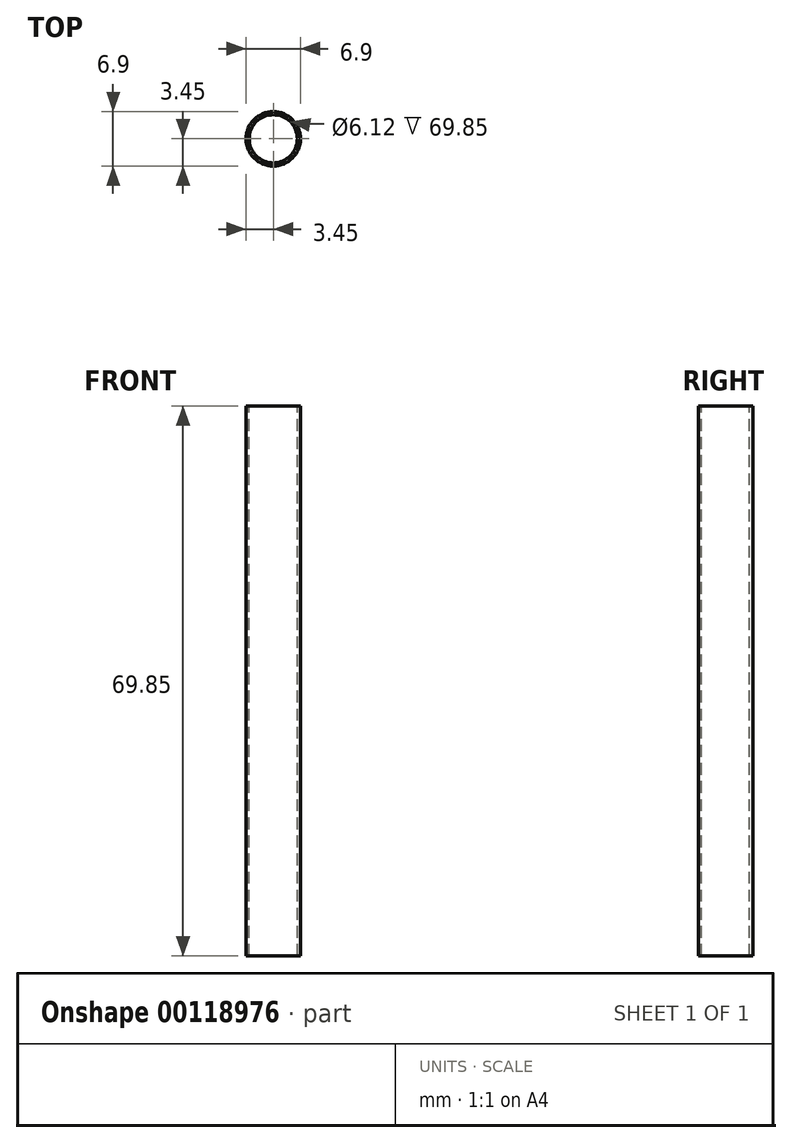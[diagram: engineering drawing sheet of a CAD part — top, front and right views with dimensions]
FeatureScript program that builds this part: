
annotation { "Feature Type Name" : "Feature", "Feature Type Description" : "" }
export const myFeature = defineFeature(function(context is Context, id is Id, definition is map)
    precondition{}
    {
        {
            var Q0;
            Q0=qCreatedBy(makeId("Top.planeOp"),FACE);
            var sketch = newSketch(context, id + "F0", { "sketchPlane" : qUnion([Q0])});
            skCircle(sketch, "E0", {"center": v(0, 0) * mm, "radius": 3.45 * mm});
            skSolve(sketch);
        }
        {
            var Q0;
            Q0=makeQuery(id+"F0.imprint","IMPRINT",FACE,{"disambiguationData":[TD([[makeQuery(id+"F0.imprint","IMPRINT",EDGE,{"derivedFrom":sQuery(id+"F0.wireOp",EDGE,"E0")}),1.0]])]});
            var Q1;
            Q1=sQuery(id+"F0.wireOp",EDGE,"E0");
            extrude(context, id + "F1", {"entities" : qUnion([Q0]), "surfaceEntities" : qUnion([Q1]), "depth" : 69.85 * mm});
        }
        {
            var Q0;
            Q0=makeQuery(id+"F1.opExtrude","CAP_FACE",FACE,{"disambiguationData":[OSD([sQuery(id+"F0.wireOp",EDGE,"E0")])],"isStart":false});
            var sketch = newSketch(context, id + "F2", { "sketchPlane" : qUnion([Q0])});
            skCircle(sketch, "E1", {"center": v(0, 0) * mm, "radius": 3.06 * mm});
            skSolve(sketch);
        }
        {
            var Q0;
            Q0 = qSketchRegion(id + "F2", true);
            extrude(context, id + "F3", {"entities" : qUnion([Q0]), "operationType" : NewBodyOperationType.REMOVE, "oppositeDirection" : true, "depth" : 96.78 * mm});
        }
    });
